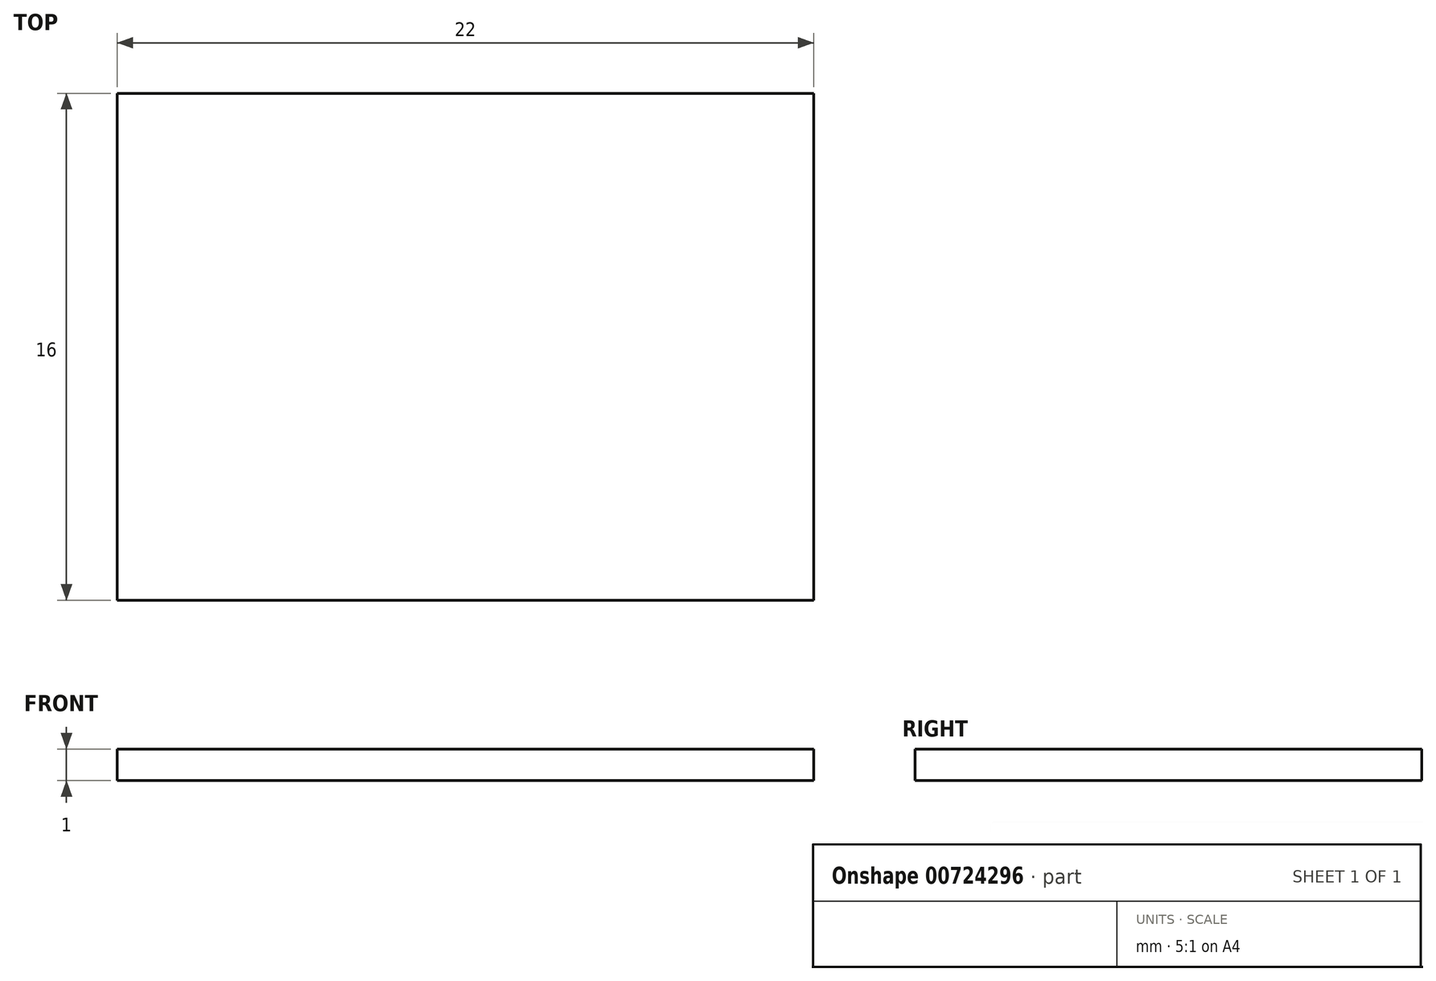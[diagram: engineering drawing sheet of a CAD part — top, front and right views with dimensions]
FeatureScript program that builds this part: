
annotation { "Feature Type Name" : "Feature", "Feature Type Description" : "" }
export const myFeature = defineFeature(function(context is Context, id is Id, definition is map)
    precondition{}
    {
        {
            var Q0;
            Q0=qCreatedBy(makeId("Top.planeOp"),FACE);
            var sketch = newSketch(context, id + "F0", { "sketchPlane" : qUnion([Q0])});
            skLineSegment(sketch, "E0.bottom", {"start": v(-11, 8) * mm, "end": v(11, 8) * mm});
            skLineSegment(sketch, "E0.top", {"start": v(-11, -8) * mm, "end": v(11, -8) * mm});
            skLineSegment(sketch, "E0.left", {"start": v(-11, 8) * mm, "end": v(-11, -8) * mm});
            skLineSegment(sketch, "E0.right", {"start": v(11, 8) * mm, "end": v(11, -8) * mm});
            skSolve(sketch);
        }
        {
            var Q0;
            Q0=qSketchRegion(id+"F0",true);
            extrude(context, id + "F1", {"entities" : qUnion([Q0]), "depth" : 1 * mm, "offsetDistance" : 25 * mm});
        }
    });
